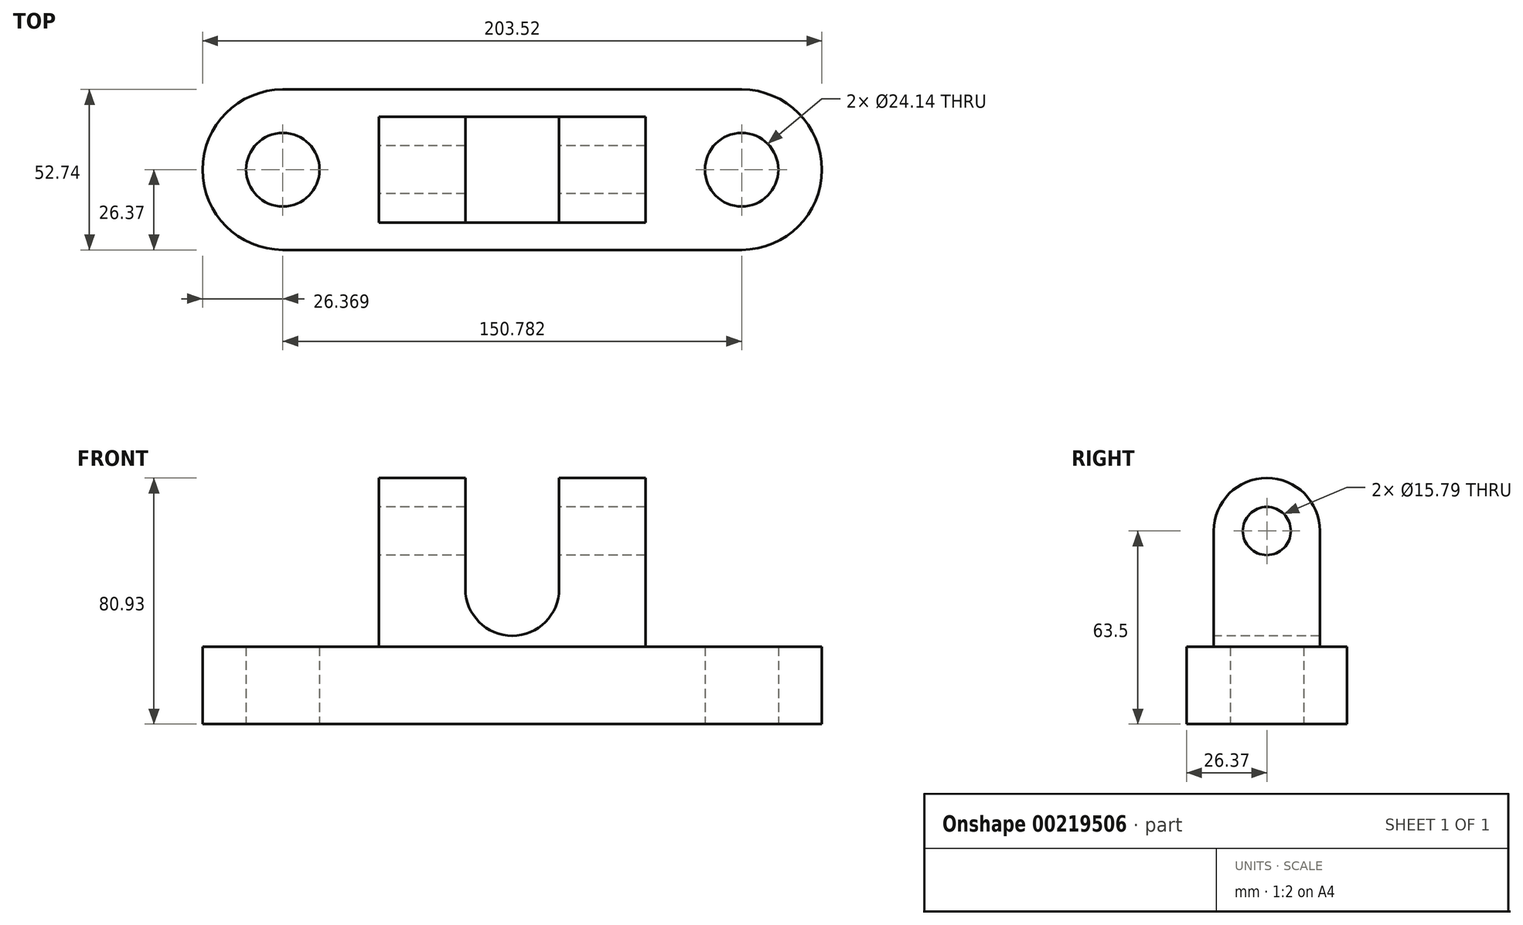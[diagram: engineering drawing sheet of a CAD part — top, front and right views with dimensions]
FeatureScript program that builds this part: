
annotation { "Feature Type Name" : "Feature", "Feature Type Description" : "" }
export const myFeature = defineFeature(function(context is Context, id is Id, definition is map)
    precondition{}
    {
        {
            var Q0;
            Q0=qCreatedBy(makeId("Top.planeOp"),FACE);
            var sketch = newSketch(context, id + "F0", { "sketchPlane" : qUnion([Q0])});
            skLineSegment(sketch, "E0.bottom", {"start": v(75.4, 26.37) * mm, "end": v(-75.4, 26.37) * mm});
            skLineSegment(sketch, "E0.top", {"start": v(75.4, -26.37) * mm, "end": v(-75.4, -26.37) * mm});
            skPoint(sketch, "E0.middle", {"position": v(0, 0) * mm});
            skArc(sketch, "E1", {"start": v(-75.4, 26.37) * mm, "mid": v(-101.76, 0) * mm, "end": v(-75.4, -26.37) * mm});
            skArc(sketch, "E2.MirrorCS", {"start": v(75.4, 26.37) * mm, "mid": v(101.76, 0) * mm, "end": v(75.4, -26.37) * mm});
            skCircle(sketch, "E3", {"center": v(-75.4, 0) * mm, "radius": 12.07 * mm});
            skCircle(sketch, "E4.MirrorC", {"center": v(75.4, 0) * mm, "radius": 12.07 * mm});
            skSolve(sketch);
        }
        {
            var Q0;
            Q0=makeQuery(id+"F0.imprint","IMPRINT",FACE,{"disambiguationData":[TD([[makeQuery(id+"F0.imprint","IMPRINT",EDGE,{"derivedFrom":sQuery(id+"F0.wireOp",EDGE,"E0.bottom")}),1.0]])]});
            extrude(context, id + "F1", {"entities" : qUnion([Q0]), "depth" : 25.4 * mm});
        }
        {
            var Q0;
            Q0=makeQuery(id+"F1.opExtrude","CAP_FACE",FACE,{"disambiguationData":[OSD([sQuery(id+"F0.wireOp",EDGE,"E0.bottom"),sQuery(id+"F0.wireOp",EDGE,"E0.top"),sQuery(id+"F0.wireOp",EDGE,"E1"),sQuery(id+"F0.wireOp",EDGE,"E2.MirrorCS"),sQuery(id+"F0.wireOp",EDGE,"E3"),sQuery(id+"F0.wireOp",EDGE,"E4.MirrorC")])],"isStart":false});
            var sketch = newSketch(context, id + "F2", { "sketchPlane" : qUnion([Q0])});
            skLineSegment(sketch, "E5.bottom", {"start": v(-43.8, 17.43) * mm, "end": v(43.8, 17.43) * mm});
            skLineSegment(sketch, "E5.top", {"start": v(-43.8, -17.43) * mm, "end": v(43.8, -17.43) * mm});
            skLineSegment(sketch, "E5.left", {"start": v(-43.8, 17.43) * mm, "end": v(-43.8, -17.43) * mm});
            skLineSegment(sketch, "E5.right", {"start": v(43.8, 17.43) * mm, "end": v(43.8, -17.43) * mm});
            skPoint(sketch, "E5.middle", {"position": v(0, 0) * mm});
            skSolve(sketch);
        }
        {
            var Q0;
            Q0 = qSketchRegion(id + "F2", true);
            extrude(context, id + "F3", {"entities" : qUnion([Q0]), "operationType" : NewBodyOperationType.ADD, "depth" : 38.1 * mm});
        }
        {
            var Q0;
            Q0=makeQuery(id+"F3.opExtrude","SWEPT_FACE",FACE,{"disambiguationData":[OSD([sQuery(id+"F2.wireOp",EDGE,"E5.left")])]});
            var sketch = newSketch(context, id + "F4", { "sketchPlane" : qUnion([Q0])});
            skArc(sketch, "E6", {"start": v(17.43, 63.5) * mm, "mid": v(0, 80.93) * mm, "end": v(-17.43, 63.5) * mm});
            skSolve(sketch);
        }
        {
            var Q0;
            Q0 = qSketchRegion(id + "F4", true);
            var Q1;
            Q1=makeQuery(id+"F4.imprint","IMPRINT",FACE,{"disambiguationData":[TD([[makeQuery(id+"F4.imprint","IMPRINT",EDGE,{"derivedFrom":sQuery(id+"F4.wireOp",EDGE,"E6")}),1.0]])]});
            extrude(context, id + "F5", {"entities" : qUnion([Q0, Q1]), "operationType" : NewBodyOperationType.ADD, "oppositeDirection" : true, "depth" : 95.5 * mm});
        }
        {
            var Q0;
            {var subQ0=sQuery(id+"F2.wireOp",EDGE,"E5.left");Q0=makeQuery(id+"F5.boolean.opBoolean","MERGE",FACE,{"derivedFrom":[makeQuery(id+"F3.opExtrude","SWEPT_FACE",FACE,{"disambiguationData":[OSD([subQ0])]}),makeQuery(id+"F5.opExtrude","CAP_FACE",FACE,{"disambiguationData":[OSD([subQ0,sQuery(id+"F4.wireOp",EDGE,"E6")])],"isStart":true})]});}
            var sketch = newSketch(context, id + "F6", { "sketchPlane" : qUnion([Q0])});
            skCircle(sketch, "E7", {"center": v(0, 63.5) * mm, "radius": 7.9 * mm});
            skSolve(sketch);
        }
        {
            var Q0;
            Q0 = qSketchRegion(id + "F6", true);
            extrude(context, id + "F7", {"entities" : qUnion([Q0]), "operationType" : NewBodyOperationType.REMOVE, "oppositeDirection" : true, "depth" : 137.16 * mm});
        }
        {
            var Q0;
            Q0=makeQuery(id+"F3.opExtrude","SWEPT_FACE",FACE,{"disambiguationData":[OSD([sQuery(id+"F2.wireOp",EDGE,"E5.top")])]});
            var sketch = newSketch(context, id + "F8", { "sketchPlane" : qUnion([Q0])});
            skArc(sketch, "E8", {"start": v(-15.39, 44.45) * mm, "mid": v(0, 29.06) * mm, "end": v(15.39, 44.45) * mm});
            skLineSegment(sketch, "E9", {"start": v(15.39, 44.45) * mm, "end": v(15.39, 88.35) * mm});
            skLineSegment(sketch, "E10", {"start": v(-15.39, 44.45) * mm, "end": v(-15.39, 88.35) * mm});
            skLineSegment(sketch, "E11", {"start": v(-15.39, 88.35) * mm, "end": v(15.39, 88.35) * mm});
            skSolve(sketch);
        }
        {
            var Q0;
            Q0 = qSketchRegion(id + "F8", true);
            extrude(context, id + "F9", {"entities" : qUnion([Q0]), "operationType" : NewBodyOperationType.REMOVE, "oppositeDirection" : true, "depth" : 43.18 * mm});
        }
        {
            var Q0;
            Q0=makeQuery(id+"F3.opExtrude","SWEPT_FACE",FACE,{"disambiguationData":[OSD([sQuery(id+"F2.wireOp",EDGE,"E5.top")])]});
            var sketch = newSketch(context, id + "F10", { "sketchPlane" : qUnion([Q0])});
            skLineSegment(sketch, "E12.bottom", {"start": v(43.8, 25.4) * mm, "end": v(58.68, 25.4) * mm});
            skLineSegment(sketch, "E12.top", {"start": v(43.8, 84.25) * mm, "end": v(58.68, 84.25) * mm});
            skLineSegment(sketch, "E12.left", {"start": v(43.8, 25.4) * mm, "end": v(43.8, 84.25) * mm});
            skLineSegment(sketch, "E12.right", {"start": v(58.68, 25.4) * mm, "end": v(58.68, 84.25) * mm});
            skSolve(sketch);
        }
        {
            var Q0;
            Q0 = qSketchRegion(id + "F10", true);
            extrude(context, id + "F11", {"entities" : qUnion([Q0]), "operationType" : NewBodyOperationType.REMOVE, "oppositeDirection" : true, "depth" : 63.25 * mm});
        }
    });
